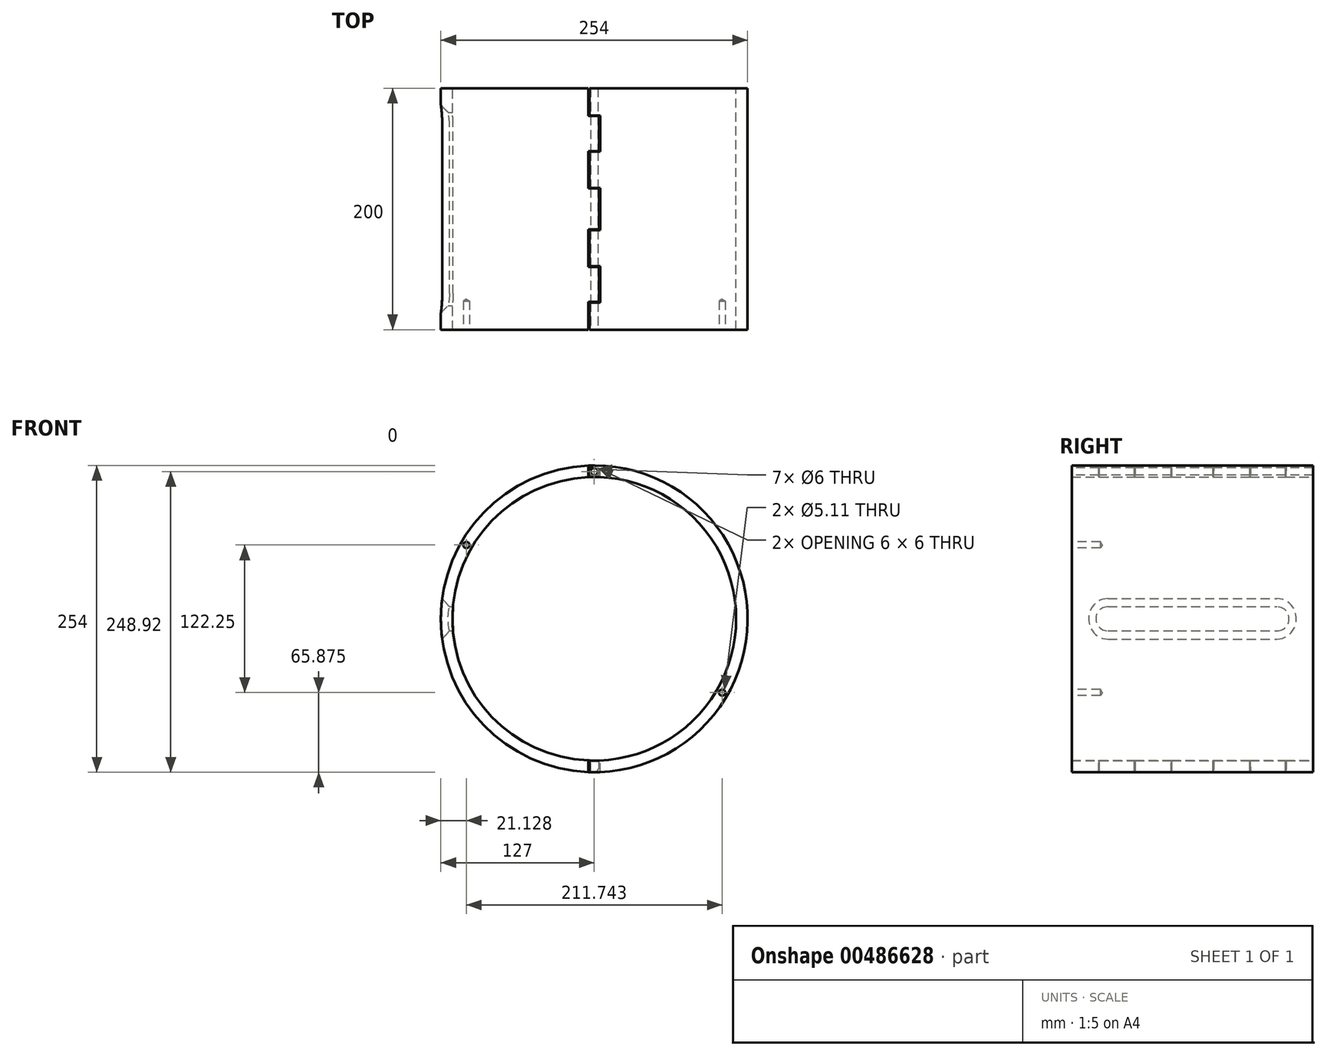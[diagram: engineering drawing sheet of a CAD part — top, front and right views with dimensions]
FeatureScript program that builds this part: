
annotation { "Feature Type Name" : "Feature", "Feature Type Description" : "" }
export const myFeature = defineFeature(function(context is Context, id is Id, definition is map)
    precondition{}
    {
        {
            var Q0;
            Q0=qCreatedBy(makeId("Front.planeOp"),FACE);
            var sketch = newSketch(context, id + "F0", { "sketchPlane" : qUnion([Q0])});
            skCircle(sketch, "E0", {"center": v(0, 0) * mm, "radius": 117.42 * mm});
            skCircle(sketch, "E1", {"center": v(0, 0) * mm, "radius": 127 * mm});
            skSolve(sketch);
        }
        {
            var Q0;
            Q0=makeQuery(id+"F0.imprint","IMPRINT",FACE,{"disambiguationData":[TD([[makeQuery(id+"F0.imprint","IMPRINT",EDGE,{"derivedFrom":sQuery(id+"F0.wireOp",EDGE,"E0")}),-1.0]])]});
            extrude(context, id + "F1", {"entities" : qUnion([Q0]), "endBound" : BoundingType.SYMMETRIC, "depth" : 200 * mm});
        }
        {
            var Q0;
            Q0=qCreatedBy(makeId("Front.planeOp"),FACE);
            var sketch = newSketch(context, id + "F2", { "sketchPlane" : qUnion([Q0])});
            skLineSegment(sketch, "E2", {"start": v(0, 0) * mm, "end": v(0, 160.57) * mm, "construction": true});
            skSolve(sketch);
        }
        {
            var Q0;
            Q0=makeQuery(id+"F1.opExtrude","CAP_FACE",FACE,{"disambiguationData":[OSD([sQuery(id+"F0.wireOp",EDGE,"E0"),sQuery(id+"F0.wireOp",EDGE,"E1")])],"isStart":false});
            var sketch = newSketch(context, id + "F3", { "sketchPlane" : qUnion([Q0])});
            skCircle(sketch, "E3", {"center": v(0, 121.92) * mm, "radius": 3 * mm});
            skSolve(sketch);
        }
        {
            var Q0;
            Q0=makeQuery(id+"F3.imprint","IMPRINT",FACE,{"disambiguationData":[TD([[makeQuery(id+"F3.imprint","IMPRINT",EDGE,{"derivedFrom":sQuery(id+"F3.wireOp",EDGE,"E3")}),1.0]])]});
            extrude(context, id + "F4", {"entities" : qUnion([Q0]), "operationType" : NewBodyOperationType.REMOVE, "endBound" : BoundingType.THROUGH_ALL, "oppositeDirection" : true, "depth" : 25 * mm});
        }
        {
            var Q0;
            Q0=qCreatedBy(makeId("Top.planeOp"),FACE);
            var sketch = newSketch(context, id + "F5", { "sketchPlane" : qUnion([Q0])});
            skLineSegment(sketch, "E4", {"start": v(0, 100.89) * mm, "end": v(0, -112.88) * mm, "construction": true});
            skLineSegment(sketch, "E5", {"start": v(-85.43, 0) * mm, "end": v(71.36, 0) * mm, "construction": true});
            skLineSegment(sketch, "E6", {"start": v(-4, 104.48) * mm, "end": v(-4, 77.5) * mm});
            skLineSegment(sketch, "E7", {"start": v(4, 77) * mm, "end": v(4, 48) * mm});
            skLineSegment(sketch, "E8", {"start": v(5, 47.5) * mm, "end": v(-4, 47.5) * mm});
            skLineSegment(sketch, "E9", {"start": v(-4, 47.5) * mm, "end": v(-4, 17.5) * mm});
            skLineSegment(sketch, "E10", {"start": v(-4, 17.5) * mm, "end": v(5, 17.5) * mm});
            skLineSegment(sketch, "E11.0", {"start": v(-5, 104.48) * mm, "end": v(-5, 77) * mm});
            skLineSegment(sketch, "E12.0", {"start": v(5, 77.5) * mm, "end": v(5, 47.5) * mm});
            skLineSegment(sketch, "E13.0", {"start": v(-5, 48) * mm, "end": v(-5, 17) * mm});
            skLineSegment(sketch, "E14.0", {"start": v(4, 48) * mm, "end": v(-5, 48) * mm});
            skLineSegment(sketch, "E15", {"start": v(-5, 17) * mm, "end": v(4, 17) * mm});
            skPoint(sketch, "E16.orphan", {"position": v(-5, 17.5) * mm});
            skLineSegment(sketch, "E17.MirrorCS", {"start": v(-5, -17) * mm, "end": v(4, -17) * mm});
            skLineSegment(sketch, "E18.MirrorCS", {"start": v(5, -47.5) * mm, "end": v(-4, -47.5) * mm});
            skLineSegment(sketch, "E19.MirrorCS", {"start": v(4, -48) * mm, "end": v(-5, -48) * mm});
            skLineSegment(sketch, "E20.MirrorCS", {"start": v(-5, -48) * mm, "end": v(-5, -17) * mm});
            skLineSegment(sketch, "E21.MirrorCS", {"start": v(-4, -104.48) * mm, "end": v(-4, -77.5) * mm});
            skLineSegment(sketch, "E22.MirrorCS", {"start": v(-4, -77.5) * mm, "end": v(5, -77.5) * mm});
            skLineSegment(sketch, "E23.MirrorCS", {"start": v(5, -77.5) * mm, "end": v(5, -47.5) * mm});
            skLineSegment(sketch, "E24.MirrorCS", {"start": v(-4, -47.5) * mm, "end": v(-4, -17.5) * mm});
            skLineSegment(sketch, "E25.MirrorCS", {"start": v(-5, -104.48) * mm, "end": v(-5, -77) * mm});
            skLineSegment(sketch, "E26.MirrorCS", {"start": v(-5, -77) * mm, "end": v(4, -77) * mm});
            skLineSegment(sketch, "E27.MirrorCS", {"start": v(4, -77) * mm, "end": v(4, -48) * mm});
            skLineSegment(sketch, "E28.MirrorCS", {"start": v(-4, -17.5) * mm, "end": v(5, -17.5) * mm});
            skLineSegment(sketch, "E29", {"start": v(-5, 104.48) * mm, "end": v(-4, 104.48) * mm});
            skLineSegment(sketch, "E30", {"start": v(-5, -104.48) * mm, "end": v(-4, -104.48) * mm});
            skLineSegment(sketch, "E31", {"start": v(-5, 77) * mm, "end": v(4, 77) * mm});
            skLineSegment(sketch, "E32", {"start": v(-4, 77.5) * mm, "end": v(5, 77.5) * mm});
            skLineSegment(sketch, "E33", {"start": v(4, -17) * mm, "end": v(4, 17) * mm});
            skLineSegment(sketch, "E34", {"start": v(5, -17.5) * mm, "end": v(5, 17.5) * mm});
            skSolve(sketch);
        }
        {
            var Q0;
            Q0=makeQuery(id+"F5.imprint","IMPRINT",FACE,{"disambiguationData":[TD([[makeQuery(id+"F5.imprint","IMPRINT",EDGE,{"derivedFrom":sQuery(id+"F5.wireOp",EDGE,"E6")}),-1.0]])]});
            extrude(context, id + "F6", {"entities" : qUnion([Q0]), "operationType" : NewBodyOperationType.REMOVE, "endBound" : BoundingType.SYMMETRIC, "oppositeDirection" : true, "depth" : 300 * mm});
        }
        {
            var Q0;
            Q0=makeQuery(id+"F6.boolean.opBoolean","INTERSECT",EDGE,{"disambiguationData":[OD(1.0)],"derivedFrom":[makeQuery(id+"F1.opExtrude","SWEPT_FACE",FACE,{"disambiguationData":[OSD([sQuery(id+"F0.wireOp",EDGE,"E1")])]}),makeQuery(id+"F6.opExtrude","SWEPT_FACE",FACE,{"disambiguationData":[OSD([sQuery(id+"F5.wireOp",EDGE,"E21.MirrorCS")])]})]});
            var Q1;
            Q1=makeQuery(id+"F6.boolean.opBoolean","INTERSECT",EDGE,{"disambiguationData":[OD(1.0)],"derivedFrom":[makeQuery(id+"F1.opExtrude","SWEPT_FACE",FACE,{"disambiguationData":[OSD([sQuery(id+"F0.wireOp",EDGE,"E1")])]}),makeQuery(id+"F6.opExtrude","SWEPT_FACE",FACE,{"disambiguationData":[OSD([sQuery(id+"F5.wireOp",EDGE,"E24.MirrorCS")])]})]});
            var Q2;
            Q2=makeQuery(id+"F6.boolean.opBoolean","INTERSECT",EDGE,{"disambiguationData":[OD(1.0)],"derivedFrom":[makeQuery(id+"F1.opExtrude","SWEPT_FACE",FACE,{"disambiguationData":[OSD([sQuery(id+"F0.wireOp",EDGE,"E1")])]}),makeQuery(id+"F6.opExtrude","SWEPT_FACE",FACE,{"disambiguationData":[OSD([sQuery(id+"F5.wireOp",EDGE,"E9")])]})]});
            var Q3;
            Q3=makeQuery(id+"F6.boolean.opBoolean","INTERSECT",EDGE,{"disambiguationData":[OD(1.0)],"derivedFrom":[makeQuery(id+"F1.opExtrude","SWEPT_FACE",FACE,{"disambiguationData":[OSD([sQuery(id+"F0.wireOp",EDGE,"E1")])]}),makeQuery(id+"F6.opExtrude","SWEPT_FACE",FACE,{"disambiguationData":[OSD([sQuery(id+"F5.wireOp",EDGE,"E6")])]})]});
            fillet(context, id + "F7", {"entities" : qUnion([Q0, Q1, Q2, Q3]), "radius" : 4.5 * mm, "tangentPropagation" : true, "allowEdgeOverflow" : false});
        }
        {
            var Q0;
            Q0=makeQuery(id+"F6.boolean.opBoolean","INTERSECT",EDGE,{"disambiguationData":[OD(0.0)],"derivedFrom":[makeQuery(id+"F1.opExtrude","SWEPT_FACE",FACE,{"disambiguationData":[OSD([sQuery(id+"F0.wireOp",EDGE,"E1")])]}),makeQuery(id+"F6.opExtrude","SWEPT_FACE",FACE,{"disambiguationData":[OSD([sQuery(id+"F5.wireOp",EDGE,"E27.MirrorCS")])]})]});
            var Q1;
            Q1=makeQuery(id+"F6.boolean.opBoolean","INTERSECT",EDGE,{"disambiguationData":[OD(0.0)],"derivedFrom":[makeQuery(id+"F1.opExtrude","SWEPT_FACE",FACE,{"disambiguationData":[OSD([sQuery(id+"F0.wireOp",EDGE,"E1")])]}),makeQuery(id+"F6.opExtrude","SWEPT_FACE",FACE,{"disambiguationData":[OSD([sQuery(id+"F5.wireOp",EDGE,"E33")])]})]});
            var Q2;
            Q2=makeQuery(id+"F6.boolean.opBoolean","INTERSECT",EDGE,{"disambiguationData":[OD(0.0)],"derivedFrom":[makeQuery(id+"F1.opExtrude","SWEPT_FACE",FACE,{"disambiguationData":[OSD([sQuery(id+"F0.wireOp",EDGE,"E1")])]}),makeQuery(id+"F6.opExtrude","SWEPT_FACE",FACE,{"disambiguationData":[OSD([sQuery(id+"F5.wireOp",EDGE,"E7")])]})]});
            fillet(context, id + "F8", {"entities" : qUnion([Q0, Q1, Q2]), "radius" : 4.5 * mm, "tangentPropagation" : true, "allowEdgeOverflow" : false});
        }
        {
            var Q0;
            Q0=makeQuery(id+"F6.boolean.opBoolean","COPY",EDGE,{"disambiguationData":[OD(0.0)],"derivedFrom":makeQuery(id+"F6.opExtrude","SWEPT_EDGE",EDGE,{"disambiguationData":[OSD([sQuery(id+"F5.wireOp",EDGE,"E9"),sQuery(id+"F5.wireOp",EDGE,"E10")])]})});
            var Q1;
            Q1=makeQuery(id+"F6.boolean.opBoolean","COPY",EDGE,{"disambiguationData":[OD(0.0)],"derivedFrom":makeQuery(id+"F6.opExtrude","SWEPT_EDGE",EDGE,{"disambiguationData":[OSD([sQuery(id+"F5.wireOp",EDGE,"E18.MirrorCS"),sQuery(id+"F5.wireOp",EDGE,"E24.MirrorCS")])]})});
            var Q2;
            Q2=makeQuery(id+"F6.boolean.opBoolean","COPY",EDGE,{"disambiguationData":[OD(0.0)],"derivedFrom":makeQuery(id+"F6.opExtrude","SWEPT_EDGE",EDGE,{"disambiguationData":[OSD([sQuery(id+"F5.wireOp",EDGE,"E6"),sQuery(id+"F5.wireOp",EDGE,"E32")])]})});
            chamfer(context, id + "F9", {"entities" : qUnion([Q0, Q1, Q2]), "chamferType" : ChamferType.OFFSET_ANGLE, "width" : 1 * mm, "oppositeDirection" : true, "angle" : 15 * degree, "tangentPropagation" : true});
        }
        {
            var Q0;
            Q0=makeQuery(id+"F6.boolean.opBoolean","COPY",EDGE,{"disambiguationData":[OD(0.0)],"derivedFrom":makeQuery(id+"F6.opExtrude","SWEPT_EDGE",EDGE,{"disambiguationData":[OSD([sQuery(id+"F5.wireOp",EDGE,"E8"),sQuery(id+"F5.wireOp",EDGE,"E9")])]})});
            var Q1;
            Q1=makeQuery(id+"F6.boolean.opBoolean","COPY",EDGE,{"disambiguationData":[OD(0.0)],"derivedFrom":makeQuery(id+"F6.opExtrude","SWEPT_EDGE",EDGE,{"disambiguationData":[OSD([sQuery(id+"F5.wireOp",EDGE,"E24.MirrorCS"),sQuery(id+"F5.wireOp",EDGE,"E28.MirrorCS")])]})});
            var Q2;
            Q2=makeQuery(id+"F6.boolean.opBoolean","COPY",EDGE,{"disambiguationData":[OD(0.0)],"derivedFrom":makeQuery(id+"F6.opExtrude","SWEPT_EDGE",EDGE,{"disambiguationData":[OSD([sQuery(id+"F5.wireOp",EDGE,"E21.MirrorCS"),sQuery(id+"F5.wireOp",EDGE,"E22.MirrorCS")])]})});
            chamfer(context, id + "F10", {"entities" : qUnion([Q0, Q1, Q2]), "chamferType" : ChamferType.OFFSET_ANGLE, "width" : 1 * mm, "oppositeDirection" : false, "angle" : 15 * degree, "tangentPropagation" : true});
        }
        {
            var Q0;
            Q0=qCreatedBy(makeId("Right.planeOp"),FACE);
            var sketch = newSketch(context, id + "F11", { "sketchPlane" : qUnion([Q0])});
            skLineSegment(sketch, "E35", {"start": v(-116.8, 0) * mm, "end": v(135.68, 0) * mm, "construction": true});
            skArc(sketch, "E36", {"start": v(-70, 10) * mm, "mid": v(-80, 0) * mm, "end": v(-70, -10) * mm});
            skArc(sketch, "E37", {"start": v(70, -10) * mm, "mid": v(80, 0) * mm, "end": v(70, 10) * mm});
            skLineSegment(sketch, "E38", {"start": v(-70, 10) * mm, "end": v(70, 10) * mm});
            skLineSegment(sketch, "E39", {"start": v(-70, -10) * mm, "end": v(70, -10) * mm});
            skSolve(sketch);
        }
        {
            var Q0;
            Q0=makeQuery(id+"F11.imprint","IMPRINT",FACE,{"disambiguationData":[TD([[makeQuery(id+"F11.imprint","IMPRINT",EDGE,{"derivedFrom":sQuery(id+"F11.wireOp",EDGE,"E36")}),1.0]])]});
            extrude(context, id + "F12", {"entities" : qUnion([Q0]), "operationType" : NewBodyOperationType.REMOVE, "oppositeDirection" : true, "depth" : 300 * mm});
        }
        {
            var Q0;
            {var subQ0=sQuery(id+"F0.wireOp",EDGE,"E1");Q0=makeQuery(id+"F12.boolean.opBoolean","INTERSECT",EDGE,{"derivedFrom":[makeQuery(id+"F6.boolean.opBoolean","SPLIT",FACE,{"disambiguationData":[TD([makeQuery(id+"F6.opExtrude","SWEPT_FACE",FACE,{"disambiguationData":[OSD([sQuery(id+"F5.wireOp",EDGE,"E7")])]})])],"derivedFrom":makeQuery(id+"F1.opExtrude","SWEPT_FACE",FACE,{"disambiguationData":[OSD([subQ0])]})}),makeQuery(id+"F12.opExtrude","SWEPT_FACE",FACE,{"disambiguationData":[OSD([sQuery(id+"F11.wireOp",EDGE,"E39")])]})]});}
            chamfer(context, id + "F13", {"entities" : qUnion([Q0]), "width" : 6 * mm, "tangentPropagation" : true});
        }
        {
            var Q0;
            {var subQ0=sQuery(id+"F0.wireOp",EDGE,"E0");var subQ1=sQuery(id+"F0.wireOp",EDGE,"E1");Q0=makeQuery(id+"F6.boolean.opBoolean","SPLIT",FACE,{"disambiguationData":[TD([makeQuery(id+"F6.opExtrude","SWEPT_FACE",FACE,{"disambiguationData":[OSD([sQuery(id+"F5.wireOp",EDGE,"E25.MirrorCS")])]})])],"derivedFrom":makeQuery(id+"F1.opExtrude","CAP_FACE",FACE,{"disambiguationData":[OSD([subQ0,subQ1])],"isStart":false})});}
            var sketch = newSketch(context, id + "F14", { "sketchPlane" : qUnion([Q0])});
            skCircle(sketch, "E40", {"center": v(0, 0) * mm, "radius": 122.25 * mm, "construction": true});
            skLineSegment(sketch, "E41", {"start": v(-127, 0) * mm, "end": v(129.71, 0) * mm, "construction": true});
            skPoint(sketch, "E41.endSnap0", {"position": v(-117.42, 0) * mm});
            skLineSegment(sketch, "E42", {"start": v(105.87, -61.12) * mm, "end": v(-109.99, 63.5) * mm, "construction": true});
            skPoint(sketch, "E43", {"position": v(-105.87, 61.12) * mm});
            skPoint(sketch, "E44", {"position": v(105.87, -61.12) * mm});
            skSolve(sketch);
        }
        {
            var Q0;
            Q0=sQuery(id+"F14.wireOp",VERTEX,"E43");
            var Q1;
            Q1=sQuery(id+"F14.wireOp",VERTEX,"E44");
            var Q2;
            Q2=makeQuery(id+"F6.boolean.opBoolean","SPLIT",BODY,{"disambiguationData":[OD(0.0)],"derivedFrom":makeQuery(id+"F1.opExtrude","SWEPT_BODY",BODY,{"disambiguationData":[OSD([sQuery(id+"F0.wireOp",EDGE,"E0"),sQuery(id+"F0.wireOp",EDGE,"E1")])]})});
            var Q3;
            Q3=makeQuery(id+"F6.boolean.opBoolean","SPLIT",BODY,{"disambiguationData":[OD(1.0)],"derivedFrom":makeQuery(id+"F1.opExtrude","SWEPT_BODY",BODY,{"disambiguationData":[OSD([sQuery(id+"F0.wireOp",EDGE,"E0"),sQuery(id+"F0.wireOp",EDGE,"E1")])]})});
            hole(context, id + "F15", {"style" : HoleStyle.SIMPLE, "endStyle" : HoleEndStyle.BLIND, "standardTappedOrClearance" : lookupTablePath({ "standard" : "ANSI", "engagement" : "75%", "pitch" : "20 tpi", "size" : "1/4", "type" : "Tapped" }), "standardBlindInLast" : lookupTablePath({ "standard" : "ANSI", "engagement" : "75%", "pitch" : "20 tpi", "size" : "1/4", "type" : "Tapped" }), "holeDiameter" : 5.1 * mm, "showTappedDepth" : true, "holeDepth" : 23.8 * mm, "isTappedThrough" : true, "tappedDepth" : 20 * mm, "tapClearance" : 3, "startFromSketch" : true, "locations" : qUnion([Q0, Q1]), "scope" : qUnion([Q2, Q3]), "majorDiameter" : 6.35 * mm});
        }
    });
